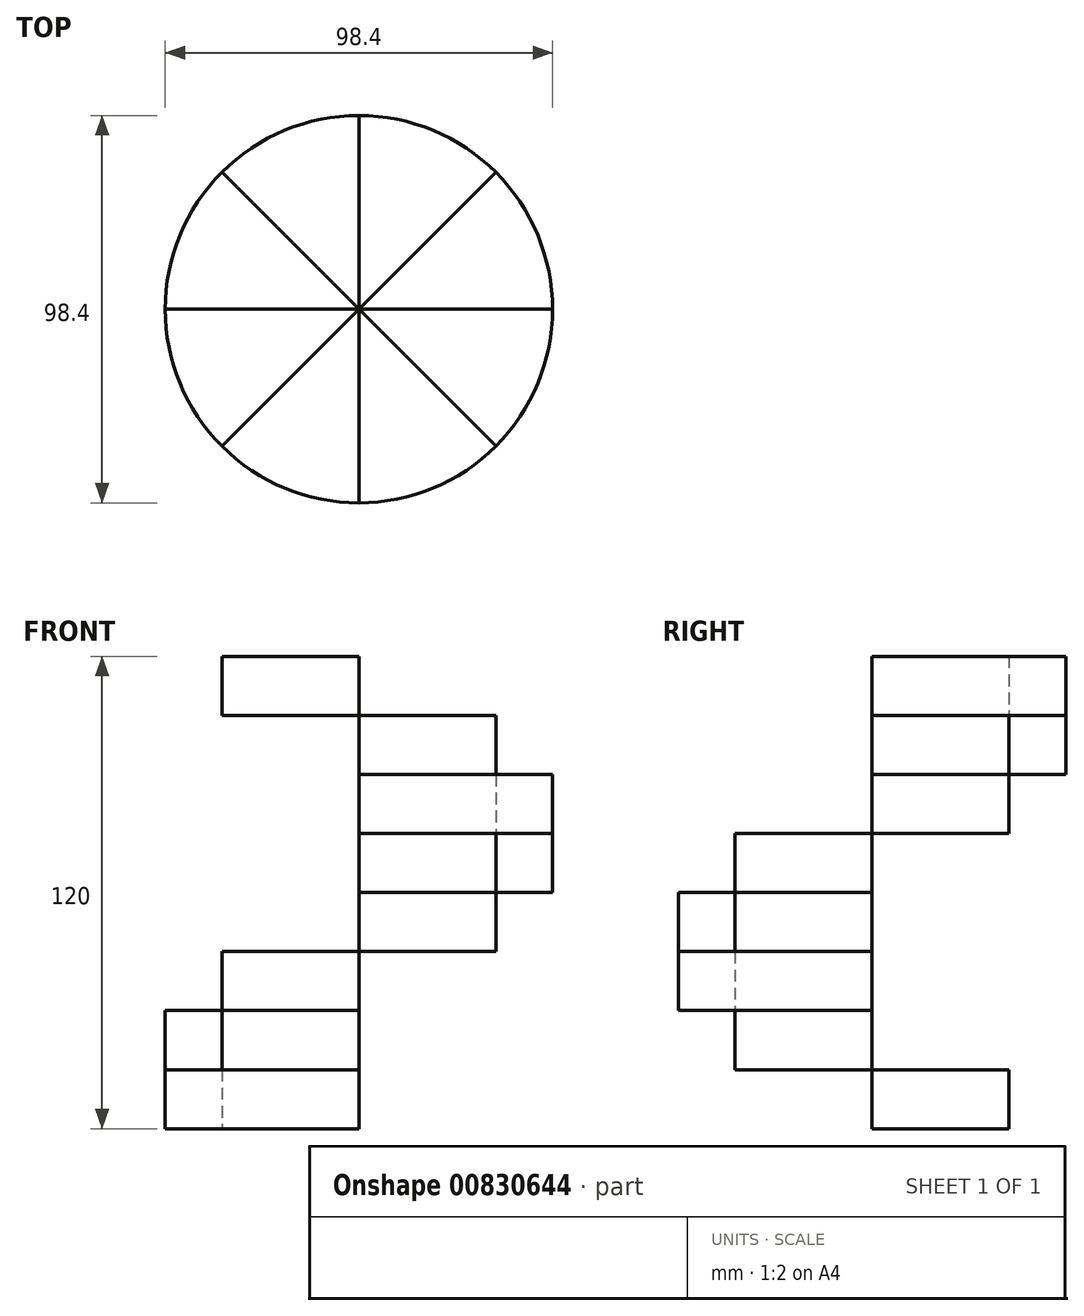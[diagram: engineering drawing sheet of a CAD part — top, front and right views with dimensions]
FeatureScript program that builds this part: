
annotation { "Feature Type Name" : "Feature", "Feature Type Description" : "" }
export const myFeature = defineFeature(function(context is Context, id is Id, definition is map)
    precondition{}
    {
        {
            var Q0;
            Q0=qCreatedBy(makeId("Top.planeOp"),FACE);
            var sketch = newSketch(context, id + "F0", { "sketchPlane" : qUnion([Q0])});
            skCircle(sketch, "E0", {"center": v(0, 0) * mm, "radius": 49.2 * mm});
            skLineSegment(sketch, "E1", {"start": v(0, 0) * mm, "end": v(49.2, 0) * mm});
            skLineSegment(sketch, "E2", {"start": v(49.2, 0) * mm, "end": v(0, 49.2) * mm});
            skLineSegment(sketch, "E3", {"start": v(0, 49.2) * mm, "end": v(-49.2, 0) * mm});
            skLineSegment(sketch, "E4", {"start": v(-49.2, 0) * mm, "end": v(0, -49.2) * mm});
            skLineSegment(sketch, "E5", {"start": v(0, -49.2) * mm, "end": v(49.2, 0) * mm});
            skLineSegment(sketch, "E6", {"start": v(-49.2, 0) * mm, "end": v(49.2, 0) * mm});
            skLineSegment(sketch, "E7", {"start": v(0, 49.2) * mm, "end": v(0, -49.2) * mm});
            skLineSegment(sketch, "E8", {"start": v(0, 0) * mm, "end": v(34.8, 34.8) * mm});
            skLineSegment(sketch, "E9", {"start": v(0, 0) * mm, "end": v(-34.8, 34.8) * mm});
            skLineSegment(sketch, "E10", {"start": v(0, 0) * mm, "end": v(-34.8, -34.8) * mm});
            skLineSegment(sketch, "E11", {"start": v(0, 0) * mm, "end": v(34.8, -34.8) * mm});
            skSolve(sketch);
        }
        {
            var Q0;
            {var subQ0=sQuery(id+"F0.wireOp",EDGE,"E6");Q0=makeQuery(id+"F0.imprint","IMPRINT",FACE,{"disambiguationData":[TD([[makeQuery(id+"F0.imprint","IMPRINT",EDGE,{"derivedFrom":subQ0}),1.0]])]});}
            var Q1;
            {var subQ1=sQuery(id+"F0.wireOp",EDGE,"E0");var subQ3=sQuery(id+"F0.wireOp",EDGE,"E9");var subQ4=makeQuery(id+"F0.imprint","INTERSECT",VERTEX,{"derivedFrom":[subQ1,subQ3]});Q1=makeQuery(id+"F0.imprint","IMPRINT",FACE,{"disambiguationData":[TD([[makeQuery(id+"F0.imprint","IMPRINT",EDGE,{"disambiguationData":[TD([[subQ4,1.0]])],"derivedFrom":subQ3}),1.0]])]});}
            extrude(context, id + "F1", {"entities" : qUnion([Q0, Q1]), "depth" : 15 * mm, "offsetDistance" : 25 * mm});
        }
        {
            var Q0;
            {var subQ0=sQuery(id+"F0.wireOp",EDGE,"E6");Q0=makeQuery(id+"F0.imprint","IMPRINT",FACE,{"disambiguationData":[TD([[makeQuery(id+"F0.imprint","IMPRINT",EDGE,{"derivedFrom":subQ0}),-1.0]])]});}
            var Q1;
            {var subQ1=sQuery(id+"F0.wireOp",EDGE,"E0");var subQ3=sQuery(id+"F0.wireOp",EDGE,"E10");var subQ4=makeQuery(id+"F0.imprint","INTERSECT",VERTEX,{"derivedFrom":[subQ1,subQ3]});Q1=makeQuery(id+"F0.imprint","IMPRINT",FACE,{"disambiguationData":[TD([[makeQuery(id+"F0.imprint","IMPRINT",EDGE,{"disambiguationData":[TD([[subQ4,1.0]])],"derivedFrom":subQ3}),-1.0]])]});}
            extrude(context, id + "F2", {"entities" : qUnion([Q0, Q1]), "operationType" : NewBodyOperationType.ADD, "depth" : 30 * mm, "offsetDistance" : 25 * mm});
        }
        {
            var Q0;
            {var subQ1=sQuery(id+"F0.wireOp",EDGE,"E4");var subQ3=sQuery(id+"F0.wireOp",EDGE,"E10");var subQ4=makeQuery(id+"F0.imprint","INTERSECT",VERTEX,{"derivedFrom":[subQ1,subQ3]});Q0=makeQuery(id+"F0.imprint","IMPRINT",FACE,{"disambiguationData":[TD([[makeQuery(id+"F0.imprint","IMPRINT",EDGE,{"disambiguationData":[TD([[subQ4,-1.0]])],"derivedFrom":subQ1}),1.0]])]});}
            var Q1;
            {var subQ1=sQuery(id+"F0.wireOp",EDGE,"E0");var subQ3=sQuery(id+"F0.wireOp",EDGE,"E10");var subQ4=makeQuery(id+"F0.imprint","INTERSECT",VERTEX,{"derivedFrom":[subQ1,subQ3]});Q1=makeQuery(id+"F0.imprint","IMPRINT",FACE,{"disambiguationData":[TD([[makeQuery(id+"F0.imprint","IMPRINT",EDGE,{"disambiguationData":[TD([[subQ4,1.0]])],"derivedFrom":subQ3}),1.0]])]});}
            extrude(context, id + "F3", {"entities" : qUnion([Q0, Q1]), "operationType" : NewBodyOperationType.ADD, "depth" : 45 * mm, "offsetDistance" : 25 * mm});
        }
        {
            var Q0;
            {var subQ1=sQuery(id+"F0.wireOp",EDGE,"E5");var subQ3=sQuery(id+"F0.wireOp",EDGE,"E11");var subQ4=makeQuery(id+"F0.imprint","INTERSECT",VERTEX,{"derivedFrom":[subQ1,subQ3]});Q0=makeQuery(id+"F0.imprint","IMPRINT",FACE,{"disambiguationData":[TD([[makeQuery(id+"F0.imprint","IMPRINT",EDGE,{"disambiguationData":[TD([[subQ4,1.0]])],"derivedFrom":subQ1}),1.0]])]});}
            var Q1;
            {var subQ1=sQuery(id+"F0.wireOp",EDGE,"E0");var subQ3=sQuery(id+"F0.wireOp",EDGE,"E11");var subQ4=makeQuery(id+"F0.imprint","INTERSECT",VERTEX,{"derivedFrom":[subQ1,subQ3]});Q1=makeQuery(id+"F0.imprint","IMPRINT",FACE,{"disambiguationData":[TD([[makeQuery(id+"F0.imprint","IMPRINT",EDGE,{"disambiguationData":[TD([[subQ4,1.0]])],"derivedFrom":subQ3}),-1.0]])]});}
            extrude(context, id + "F4", {"entities" : qUnion([Q0, Q1]), "operationType" : NewBodyOperationType.ADD, "depth" : 60 * mm, "offsetDistance" : 25 * mm});
        }
        {
            var Q0;
            {var subQ0=sQuery(id+"F0.wireOp",EDGE,"E1");Q0=makeQuery(id+"F0.imprint","IMPRINT",FACE,{"disambiguationData":[TD([[makeQuery(id+"F0.imprint","IMPRINT",EDGE,{"derivedFrom":subQ0}),-1.0]])]});}
            var Q1;
            {var subQ1=sQuery(id+"F0.wireOp",EDGE,"E0");var subQ3=sQuery(id+"F0.wireOp",EDGE,"E11");var subQ4=makeQuery(id+"F0.imprint","INTERSECT",VERTEX,{"derivedFrom":[subQ1,subQ3]});Q1=makeQuery(id+"F0.imprint","IMPRINT",FACE,{"disambiguationData":[TD([[makeQuery(id+"F0.imprint","IMPRINT",EDGE,{"disambiguationData":[TD([[subQ4,1.0]])],"derivedFrom":subQ3}),1.0]])]});}
            extrude(context, id + "F5", {"entities" : qUnion([Q0, Q1]), "operationType" : NewBodyOperationType.ADD, "depth" : 75 * mm, "offsetDistance" : 25 * mm});
        }
        {
            var Q0;
            {var subQ0=sQuery(id+"F0.wireOp",EDGE,"E1");Q0=makeQuery(id+"F0.imprint","IMPRINT",FACE,{"disambiguationData":[TD([[makeQuery(id+"F0.imprint","IMPRINT",EDGE,{"derivedFrom":subQ0}),1.0]])]});}
            var Q1;
            {var subQ1=sQuery(id+"F0.wireOp",EDGE,"E0");var subQ3=sQuery(id+"F0.wireOp",EDGE,"E8");var subQ4=makeQuery(id+"F0.imprint","INTERSECT",VERTEX,{"derivedFrom":[subQ1,subQ3]});Q1=makeQuery(id+"F0.imprint","IMPRINT",FACE,{"disambiguationData":[TD([[makeQuery(id+"F0.imprint","IMPRINT",EDGE,{"disambiguationData":[TD([[subQ4,1.0]])],"derivedFrom":subQ3}),-1.0]])]});}
            extrude(context, id + "F6", {"entities" : qUnion([Q0, Q1]), "operationType" : NewBodyOperationType.ADD, "depth" : 90 * mm, "offsetDistance" : 25 * mm});
        }
        {
            var Q0;
            {var subQ0=sQuery(id+"F0.wireOp",EDGE,"E6");Q0=makeQuery(id+"F0.imprint","IMPRINT",FACE,{"disambiguationData":[TD([[makeQuery(id+"F0.imprint","IMPRINT",EDGE,{"derivedFrom":subQ0}),-1.0]])]});}
            var Q1;
            {var subQ1=sQuery(id+"F0.wireOp",EDGE,"E0");var subQ3=sQuery(id+"F0.wireOp",EDGE,"E10");var subQ4=makeQuery(id+"F0.imprint","INTERSECT",VERTEX,{"derivedFrom":[subQ1,subQ3]});Q1=makeQuery(id+"F0.imprint","IMPRINT",FACE,{"disambiguationData":[TD([[makeQuery(id+"F0.imprint","IMPRINT",EDGE,{"disambiguationData":[TD([[subQ4,1.0]])],"derivedFrom":subQ3}),-1.0]])]});}
            extrude(context, id + "F7", {"entities" : qUnion([Q0, Q1]), "operationType" : NewBodyOperationType.REMOVE, "depth" : 15 * mm, "offsetDistance" : 25 * mm});
        }
        {
            var Q0;
            {var subQ1=sQuery(id+"F0.wireOp",EDGE,"E4");var subQ3=sQuery(id+"F0.wireOp",EDGE,"E10");var subQ4=makeQuery(id+"F0.imprint","INTERSECT",VERTEX,{"derivedFrom":[subQ1,subQ3]});Q0=makeQuery(id+"F0.imprint","IMPRINT",FACE,{"disambiguationData":[TD([[makeQuery(id+"F0.imprint","IMPRINT",EDGE,{"disambiguationData":[TD([[subQ4,-1.0]])],"derivedFrom":subQ1}),1.0]])]});}
            var Q1;
            {var subQ1=sQuery(id+"F0.wireOp",EDGE,"E0");var subQ3=sQuery(id+"F0.wireOp",EDGE,"E10");var subQ4=makeQuery(id+"F0.imprint","INTERSECT",VERTEX,{"derivedFrom":[subQ1,subQ3]});Q1=makeQuery(id+"F0.imprint","IMPRINT",FACE,{"disambiguationData":[TD([[makeQuery(id+"F0.imprint","IMPRINT",EDGE,{"disambiguationData":[TD([[subQ4,1.0]])],"derivedFrom":subQ3}),1.0]])]});}
            extrude(context, id + "F8", {"entities" : qUnion([Q0, Q1]), "operationType" : NewBodyOperationType.REMOVE, "depth" : 30 * mm, "offsetDistance" : 25 * mm});
        }
        {
            var Q0;
            {var subQ1=sQuery(id+"F0.wireOp",EDGE,"E5");var subQ3=sQuery(id+"F0.wireOp",EDGE,"E11");var subQ4=makeQuery(id+"F0.imprint","INTERSECT",VERTEX,{"derivedFrom":[subQ1,subQ3]});Q0=makeQuery(id+"F0.imprint","IMPRINT",FACE,{"disambiguationData":[TD([[makeQuery(id+"F0.imprint","IMPRINT",EDGE,{"disambiguationData":[TD([[subQ4,1.0]])],"derivedFrom":subQ1}),1.0]])]});}
            var Q1;
            {var subQ1=sQuery(id+"F0.wireOp",EDGE,"E0");var subQ3=sQuery(id+"F0.wireOp",EDGE,"E11");var subQ4=makeQuery(id+"F0.imprint","INTERSECT",VERTEX,{"derivedFrom":[subQ1,subQ3]});Q1=makeQuery(id+"F0.imprint","IMPRINT",FACE,{"disambiguationData":[TD([[makeQuery(id+"F0.imprint","IMPRINT",EDGE,{"disambiguationData":[TD([[subQ4,1.0]])],"derivedFrom":subQ3}),-1.0]])]});}
            extrude(context, id + "F9", {"entities" : qUnion([Q0, Q1]), "operationType" : NewBodyOperationType.REMOVE, "depth" : 45 * mm, "offsetDistance" : 25 * mm});
        }
        {
            var Q0;
            {var subQ0=sQuery(id+"F0.wireOp",EDGE,"E1");Q0=makeQuery(id+"F0.imprint","IMPRINT",FACE,{"disambiguationData":[TD([[makeQuery(id+"F0.imprint","IMPRINT",EDGE,{"derivedFrom":subQ0}),-1.0]])]});}
            var Q1;
            {var subQ1=sQuery(id+"F0.wireOp",EDGE,"E0");var subQ3=sQuery(id+"F0.wireOp",EDGE,"E11");var subQ4=makeQuery(id+"F0.imprint","INTERSECT",VERTEX,{"derivedFrom":[subQ1,subQ3]});Q1=makeQuery(id+"F0.imprint","IMPRINT",FACE,{"disambiguationData":[TD([[makeQuery(id+"F0.imprint","IMPRINT",EDGE,{"disambiguationData":[TD([[subQ4,1.0]])],"derivedFrom":subQ3}),1.0]])]});}
            extrude(context, id + "F10", {"entities" : qUnion([Q0, Q1]), "operationType" : NewBodyOperationType.REMOVE, "depth" : 60 * mm, "offsetDistance" : 25 * mm});
        }
        {
            var Q0;
            {var subQ0=sQuery(id+"F0.wireOp",EDGE,"E1");Q0=makeQuery(id+"F0.imprint","IMPRINT",FACE,{"disambiguationData":[TD([[makeQuery(id+"F0.imprint","IMPRINT",EDGE,{"derivedFrom":subQ0}),1.0]])]});}
            var Q1;
            {var subQ1=sQuery(id+"F0.wireOp",EDGE,"E0");var subQ3=sQuery(id+"F0.wireOp",EDGE,"E8");var subQ4=makeQuery(id+"F0.imprint","INTERSECT",VERTEX,{"derivedFrom":[subQ1,subQ3]});Q1=makeQuery(id+"F0.imprint","IMPRINT",FACE,{"disambiguationData":[TD([[makeQuery(id+"F0.imprint","IMPRINT",EDGE,{"disambiguationData":[TD([[subQ4,1.0]])],"derivedFrom":subQ3}),-1.0]])]});}
            extrude(context, id + "F11", {"entities" : qUnion([Q0, Q1]), "operationType" : NewBodyOperationType.REMOVE, "depth" : 75 * mm, "offsetDistance" : 25 * mm});
        }
        {
            var Q0;
            {var subQ1=sQuery(id+"F0.wireOp",EDGE,"E2");var subQ3=sQuery(id+"F0.wireOp",EDGE,"E8");var subQ4=makeQuery(id+"F0.imprint","INTERSECT",VERTEX,{"derivedFrom":[subQ1,subQ3]});Q0=makeQuery(id+"F0.imprint","IMPRINT",FACE,{"disambiguationData":[TD([[makeQuery(id+"F0.imprint","IMPRINT",EDGE,{"disambiguationData":[TD([[subQ4,-1.0]])],"derivedFrom":subQ1}),1.0]])]});}
            var Q1;
            {var subQ1=sQuery(id+"F0.wireOp",EDGE,"E0");var subQ3=sQuery(id+"F0.wireOp",EDGE,"E8");var subQ4=makeQuery(id+"F0.imprint","INTERSECT",VERTEX,{"derivedFrom":[subQ1,subQ3]});Q1=makeQuery(id+"F0.imprint","IMPRINT",FACE,{"disambiguationData":[TD([[makeQuery(id+"F0.imprint","IMPRINT",EDGE,{"disambiguationData":[TD([[subQ4,1.0]])],"derivedFrom":subQ3}),1.0]])]});}
            extrude(context, id + "F12", {"entities" : qUnion([Q0, Q1]), "operationType" : NewBodyOperationType.ADD, "depth" : 105 * mm, "offsetDistance" : 25 * mm});
        }
        {
            var Q0;
            {var subQ1=sQuery(id+"F0.wireOp",EDGE,"E0");var subQ3=sQuery(id+"F0.wireOp",EDGE,"E9");var subQ4=makeQuery(id+"F0.imprint","INTERSECT",VERTEX,{"derivedFrom":[subQ1,subQ3]});Q0=makeQuery(id+"F0.imprint","IMPRINT",FACE,{"disambiguationData":[TD([[makeQuery(id+"F0.imprint","IMPRINT",EDGE,{"disambiguationData":[TD([[subQ4,1.0]])],"derivedFrom":subQ3}),-1.0]])]});}
            var Q1;
            {var subQ1=sQuery(id+"F0.wireOp",EDGE,"E3");var subQ3=sQuery(id+"F0.wireOp",EDGE,"E9");var subQ4=makeQuery(id+"F0.imprint","INTERSECT",VERTEX,{"derivedFrom":[subQ1,subQ3]});Q1=makeQuery(id+"F0.imprint","IMPRINT",FACE,{"disambiguationData":[TD([[makeQuery(id+"F0.imprint","IMPRINT",EDGE,{"disambiguationData":[TD([[subQ4,1.0]])],"derivedFrom":subQ1}),1.0]])]});}
            extrude(context, id + "F13", {"entities" : qUnion([Q0, Q1]), "depth" : 120 * mm, "offsetDistance" : 25 * mm});
        }
        {
            var Q0;
            {var subQ1=sQuery(id+"F0.wireOp",EDGE,"E2");var subQ3=sQuery(id+"F0.wireOp",EDGE,"E8");var subQ4=makeQuery(id+"F0.imprint","INTERSECT",VERTEX,{"derivedFrom":[subQ1,subQ3]});Q0=makeQuery(id+"F0.imprint","IMPRINT",FACE,{"disambiguationData":[TD([[makeQuery(id+"F0.imprint","IMPRINT",EDGE,{"disambiguationData":[TD([[subQ4,-1.0]])],"derivedFrom":subQ1}),1.0]])]});}
            var Q1;
            {var subQ1=sQuery(id+"F0.wireOp",EDGE,"E0");var subQ3=sQuery(id+"F0.wireOp",EDGE,"E8");var subQ4=makeQuery(id+"F0.imprint","INTERSECT",VERTEX,{"derivedFrom":[subQ1,subQ3]});Q1=makeQuery(id+"F0.imprint","IMPRINT",FACE,{"disambiguationData":[TD([[makeQuery(id+"F0.imprint","IMPRINT",EDGE,{"disambiguationData":[TD([[subQ4,1.0]])],"derivedFrom":subQ3}),1.0]])]});}
            extrude(context, id + "F14", {"entities" : qUnion([Q0, Q1]), "operationType" : NewBodyOperationType.REMOVE, "depth" : 90 * mm, "offsetDistance" : 25 * mm});
        }
        {
            var Q0;
            {var subQ1=sQuery(id+"F0.wireOp",EDGE,"E3");var subQ3=sQuery(id+"F0.wireOp",EDGE,"E9");var subQ4=makeQuery(id+"F0.imprint","INTERSECT",VERTEX,{"derivedFrom":[subQ1,subQ3]});Q0=makeQuery(id+"F0.imprint","IMPRINT",FACE,{"disambiguationData":[TD([[makeQuery(id+"F0.imprint","IMPRINT",EDGE,{"disambiguationData":[TD([[subQ4,1.0]])],"derivedFrom":subQ1}),1.0]])]});}
            var Q1;
            {var subQ1=sQuery(id+"F0.wireOp",EDGE,"E0");var subQ3=sQuery(id+"F0.wireOp",EDGE,"E9");var subQ4=makeQuery(id+"F0.imprint","INTERSECT",VERTEX,{"derivedFrom":[subQ1,subQ3]});Q1=makeQuery(id+"F0.imprint","IMPRINT",FACE,{"disambiguationData":[TD([[makeQuery(id+"F0.imprint","IMPRINT",EDGE,{"disambiguationData":[TD([[subQ4,1.0]])],"derivedFrom":subQ3}),-1.0]])]});}
            extrude(context, id + "F15", {"entities" : qUnion([Q0, Q1]), "operationType" : NewBodyOperationType.REMOVE, "depth" : 105 * mm, "offsetDistance" : 25 * mm});
        }
    });
